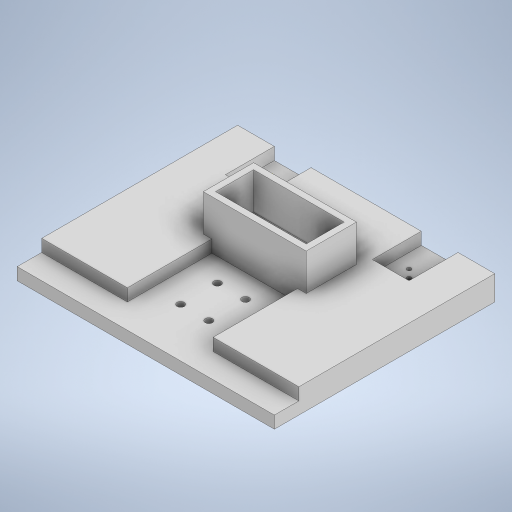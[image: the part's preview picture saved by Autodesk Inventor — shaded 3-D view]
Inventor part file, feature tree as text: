
AUTODESK INVENTOR PART (.ipt)
format: ipt  version: 2023 (Build 270158000, 158)  size: 348,672 bytes
history: native  units: mm
features: sketch x7, extrude x5, other x1, hole x1
ambient origin geometry x8: Origin, YZ Plane, XZ Plane, XY Plane, X Axis, Y Axis, Z Axis, Center Point
bodies: Body1 (feature_tree)
feature tree (14):
  other  "Sólido1"
  extrude  "Extrusión1"  Depth=180.0mm
  extrude  "Extrusión2"  Depth=20.0mm
  extrude  "Extrusión3"  Depth=20.0mm
  hole  "Agujero1"  [1 undecoded]
  extrude  "Extrusión4"  Depth=28.0mm
  extrude  "Extrusión5"  Depth=84.0mm
  sketch  "Boceto7"  dims[d24=41.0mm d25=19.0mm d26=74.0mm d27=31.0mm d28=30.0mm d29=0.0mm d30=3.5mm d32=40.0mm d33=1.75mm d34=1.75mm d35=1.75mm d36=1.75mm d37=10.0mm d38=10.0mm d39=20.0mm d40=3.5mm d41=6.0mm d42=4.0mm d43=2.0mm d44=90.0deg d45=8.0mm d46=20.594885mm d47=10.0mm d48=10.0mm d49=40.0mm d50=10.0mm d51=0.0mm d52=20.0mm d53=20.0mm d54=30.0mm d55=30.0mm d56=20.0mm d57=35.0mm d58=35.0mm d59=69.0mm d60=10.0mm d61=0.0mm]
  sketch  "Boceto1"  dims[d0=210.0mm d1=180.0mm]
  sketch  "Boceto2"  dims[d2=20.0mm d3=0.0mm d4=20.0mm d5=20.0mm d6=30.0mm d7=30.0mm]
  sketch  "Boceto3"  dims[d8=20.0mm d9=7.0mm d11=7.0mm]
  sketch  "Boceto4"  dims[d12=31.0mm d13=31.0mm]
  sketch  "Boceto5"  dims[d14=28.0mm d15=28.0mm]
  sketch  "Boceto6"  dims[d16=20.0mm d17=0.0mm d23=84.0mm]
note: 1 required parameter value undecoded (feature->parameter linkage not recoverable at this tier; creation-order binding heuristic only, values carry confidence <= 0.55)
